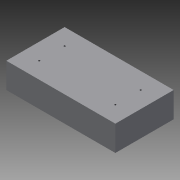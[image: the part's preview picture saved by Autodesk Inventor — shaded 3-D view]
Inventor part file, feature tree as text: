
AUTODESK INVENTOR PART (.ipt)
format: ipt  version: 2013 (Build 170138000, 138)  size: 82,432 bytes
history: native  units: mm
features: sketch x2, extrude x1, hole x1
ambient origin geometry x8: Origin, YZ Plane, XZ Plane, XY Plane, X Axis, Y Axis, Z Axis, Center Point
bodies: Solid1 (feature_tree)
feature tree (4):
  extrude  "Extrusion1"  Depth=115.0mm
  hole  "Hole1"  [1 undecoded]
  sketch  "Sketch1"  dims[d0=215.0mm d2=115.0mm]
  sketch  "Sketch2"  dims[d3=50.0mm d4=0.0mm d5=150.0mm d7=50.0mm d8=3.242mm d9=5.0mm d10=4.0mm d11=2.0mm d12=90.0deg d13=5.0mm d14=20.594885mm]
note: 1 required parameter value undecoded (feature->parameter linkage not recoverable at this tier; creation-order binding heuristic only, values carry confidence <= 0.55)
